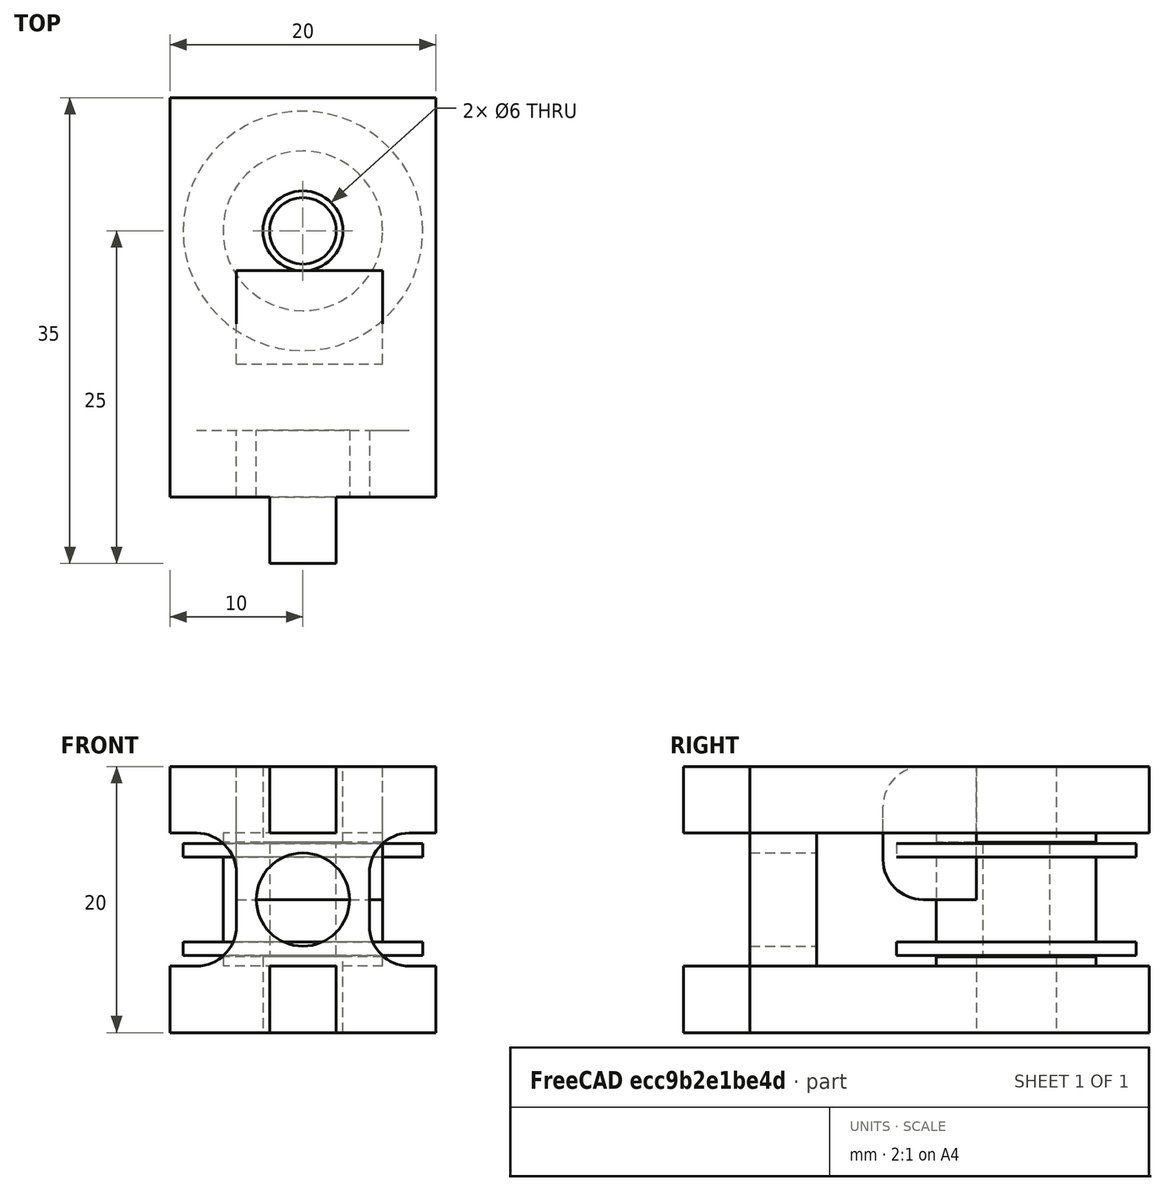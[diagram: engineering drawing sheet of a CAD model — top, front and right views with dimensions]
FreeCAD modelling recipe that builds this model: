
FCSTD DOCUMENT  (FreeCAD 0.20R29177 (Git))
Label: Poleay
License: All rights reserved
LicenseURL: http://en.wikipedia.org/wiki/All_rights_reserved
objects: Part::Cylinder×6, Part::Cut×4, Part::Box×4, Part::FeaturePython×3, Part::MultiFuse×3, Part::Refine×2, Part::Fuse×1, Spreadsheet::Sheet×1, PartDesign::FeatureBase×1, PartDesign::Fillet×1, PartDesign::Body×1
note: 26 computed .brp shape members not serialized (recipe doc carries the construction recipe); baked Part::Feature solids carry a one-line shape summary decoded from their .brp

FEATURE [Part::Cylinder] Cylinder002  label="Cilindro002"
  Angle = 360
  AttacherType = Attacher::AttachEngine3D
  FirstAngle = 0
  Height = 1
  Placement = pos=(0,0,-4.2) rot=(0,0,1;0rad)
  Radius = 9
  SecondAngle = 0
FEATURE [Part::Cylinder] Cylinder003  label="Cilindro003"
  Angle = 360
  AttacherType = Attacher::AttachEngine3D
  FirstAngle = 0
  Height = 10
  Placement = pos=(0,0,-5) rot=(0,0,1;0rad)
  Radius = 2.5
  SecondAngle = 0
FEATURE [Part::Fuse] Fusion001
  Base = -> Cylinder002
FEATURE [Part::Cut] Cut  label="Pulley"
  Base = -> Fusion001
  Placement = pos=(0,15,0) rot=(0,0,1;0rad)
  Tool = -> Cylinder003
  expr: .Placement.Base.y = Spreadsheet.viajPolea
FEATURE [Spreadsheet::Sheet] Spreadsheet
  cells = A1=Nombre; B1=Valor; A2=viajPolea; B2(viajPolea)=15; A3=tol; B3(tol)=1; A4=esp; B4(esp)=5; A5=prof; B5(prof)=20; A6=profMedio; B6(profMedio)==B5 / 2; A7=espDob; B7(espDob)==B4 * 2; A8=espMedio; B8(espMedio)==B4 / 2; A9=profMedREsp; B9(profMedREsp)==B6 - B4; A10=lonPol; B10(lonPol)==B2 + B6
FEATURE [Part::Box] Box  label="Base"
  AttacherType = Attacher::AttachEngine3D
  Height = 20
  Length = 20
  Placement = pos=(-10,-5,-10) rot=(0,0,1;0rad)
  Width = 5
  expr: .Placement.Base.x = -Spreadsheet.profMedio
  expr: .Placement.Base.y = -Spreadsheet.esp
  expr: .Placement.Base.z = -Spreadsheet.profMedio
  expr: Height = Spreadsheet.prof
  expr: Length = Spreadsheet.prof
  expr: Width = Spreadsheet.esp
FEATURE [Part::Box] Box001  label="pin0"
  AttacherType = Attacher::AttachEngine3D
  Height = 5
  Length = 5
  Placement = pos=(-2.5,-10,5) rot=(0,0,1;0rad)
  Width = 10
  expr: .Placement.Base.x = -Spreadsheet.espMedio
  expr: .Placement.Base.y = -Spreadsheet.espDob
  expr: .Placement.Base.z = Spreadsheet.profMedREsp
  expr: Height = Spreadsheet.esp
  expr: Length = Spreadsheet.esp
  expr: Width = Spreadsheet.espDob
FEATURE [Part::FeaturePython] Clone  label="pin001"  # Draft clone (typed FeaturePython)
  AttacherType = Attacher::AttachEngine3D
  Fuse = false
  Objects = -> [Box001]
  Placement = pos=(-2.5,-10,-10) rot=(0,0,1;0rad)
  Scale = (1,1,1)
  expr: .Placement.Base.y = -Spreadsheet.espDob
  expr: .Placement.Base.z = -Spreadsheet.profMedio
FEATURE [Part::Box] Box002  label="pared1"
  AttacherType = Attacher::AttachEngine3D
  Height = 5
  Length = 20
  Placement = pos=(-10,0,5) rot=(0,0,1;0rad)
  Width = 25
  expr: .Placement.Base.x = -Spreadsheet.profMedio
  expr: .Placement.Base.z = Spreadsheet.profMedREsp
  expr: Height = Spreadsheet.esp
  expr: Length = Spreadsheet.prof
  expr: Width = Spreadsheet.lonPol
FEATURE [Part::FeaturePython] Clone001  label="pared002"  # Draft clone (typed FeaturePython)
  AttacherType = Attacher::AttachEngine3D
  Fuse = false
  Objects = -> [Box002]
  Placement = pos=(-10,0,-10) rot=(0,0,1;0rad)
  Scale = (1,1,1)
  expr: .Placement.Base.z = -Spreadsheet.profMedio
FEATURE [Part::MultiFuse] Fusion
  Shapes = -> [Box,Box001,Clone,Box002,Clone001]
FEATURE [Part::Refine] Fusion002
  Source = -> Fusion
FEATURE [Part::Cylinder] Cylinder004  label="Cilindro004"
  Angle = 360
  AttacherType = Attacher::AttachEngine3D
  FirstAngle = 0
  Height = 30
  Placement = pos=(0,15,-15) rot=(0,0,1;0rad)
  Radius = 3
  SecondAngle = 0
  expr: .Placement.Base.y = Spreadsheet.viajPolea
FEATURE [Part::Box] Box007  label="Cubo005"
  AttacherType = Attacher::AttachEngine3D
  Height = 10
  Length = 11
  Placement = pos=(10,5,-5) rot=(0,0,1;0rad)
  Width = 7
FEATURE [PartDesign::FeatureBase] BaseFeature
  BaseFeature = -> Box007
FEATURE [PartDesign::Fillet] Fillet
  Base = -> BaseFeature [Edge10,Edge9]
  BaseFeature = -> BaseFeature
  Radius = 3
  SupportTransform = false
  UseAllEdges = false
FEATURE [PartDesign::Body] Body
  BaseFeature = -> Box007
  Group = -> [BaseFeature,Fillet]
  Origin = -> Origin
  Placement = pos=(-5,5,0) rot=(0,0,1;0rad)
  Tip = -> Fillet
FEATURE [Part::FeaturePython] Array  # Draft array (typed FeaturePython)
  AlwaysSyncPlacement = false
  Angle = 180
  ArrayType = 1
  Axis = (0,0,1)
  Base = -> Body
  Center = (0,0,0)
  Count = 2
  ExpandArray = false
  Fuse = false
  IntervalAxis = (0,0,0)
  IntervalX = (50,0,0)
  IntervalY = (0,50,0)
  IntervalZ = (0,0,50)
  NumberCircles = 3
  NumberPolar = 2
  NumberX = 2
  NumberY = 2
  NumberZ = 1
  Placement = pos=(0,-3,-5) rot=(0,0,1;1.5708rad)
  PlacementList = 2 placements: [(-5,5,0),(5,-5,0)]
  RadialDistance = 50
  ScaleList = (2) [(1,1,1),(1,1,1)]
  Symmetry = 1
  TangentialDistance = 25
  expr: .Placement.Base.z = -Spreadsheet.esp
FEATURE [Part::Cylinder] Cylinder  label="Cilindro"
  Angle = 360
  AttacherType = Attacher::AttachEngine3D
  FirstAngle = 0
  Height = 15
  Placement = pos=(0,5,0) rot=(1,0,0;1.5708rad)
  Radius = 3.5
  SecondAngle = 0
FEATURE [Part::Cylinder] Cylinder005  label="apoyo2"
  Angle = 360
  AttacherType = Attacher::AttachEngine3D
  FirstAngle = 0
  Height = 4
  Placement = pos=(0,0,-8.3) rot=(0,0,1;0rad)
  Radius = 6
  SecondAngle = 0
FEATURE [Part::Cylinder] Cylinder006  label="apoyo1"
  Angle = 360
  AttacherType = Attacher::AttachEngine3D
  FirstAngle = 0
  Height = 4
  Placement = pos=(0,0,4.3) rot=(0,0,1;0rad)
  Radius = 6
  SecondAngle = 0
FEATURE [Part::MultiFuse] Fusion003
  Placement = pos=(0,15,0) rot=(0,0,1;0rad)
  Shapes = -> [Cylinder005,Cylinder006]
  expr: .Placement.Base.y = Spreadsheet.viajPolea
FEATURE [Part::MultiFuse] Fusion004
  Shapes = -> [Fusion002,Fusion003]
FEATURE [Part::Refine] Fusion004001
  Source = -> Fusion004
FEATURE [Part::Cut] Cut001
  Base = -> Fusion004001
  Tool = -> Cylinder
FEATURE [Part::Cut] Cut002
  Base = -> Cut001
  Tool = -> Cylinder004
FEATURE [Part::Cut] Cut003
  Base = -> Cut002
  Tool = -> Array
